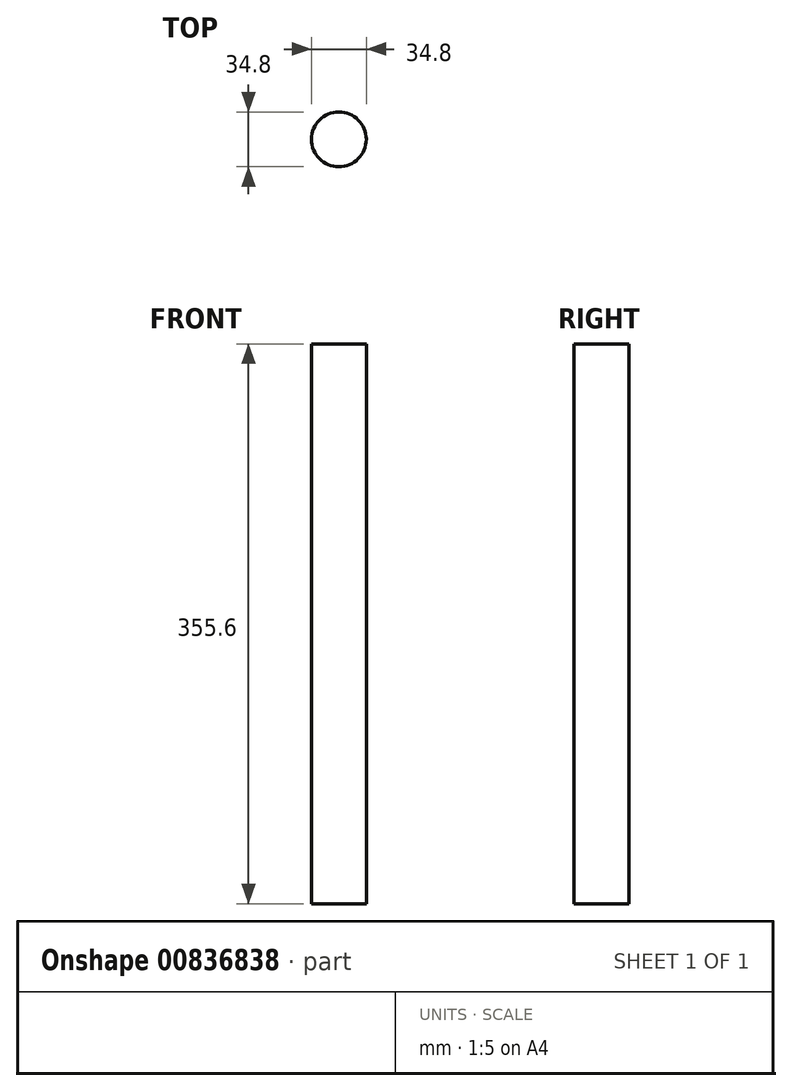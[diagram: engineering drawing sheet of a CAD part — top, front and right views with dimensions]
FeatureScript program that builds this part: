
annotation { "Feature Type Name" : "Feature", "Feature Type Description" : "" }
export const myFeature = defineFeature(function(context is Context, id is Id, definition is map)
    precondition{}
    {
        {
            var Q0;
            Q0=qCreatedBy(makeId("Top.planeOp"),FACE);
            var sketch = newSketch(context, id + "F0", { "sketchPlane" : qUnion([Q0])});
            skCircle(sketch, "E0", {"center": v(0, 0) * mm, "radius": 17.4 * mm});
            skSolve(sketch);
        }
        {
            var Q0;
            Q0=sQuery(id+"F0.wireOp",EDGE,"E0");
            extrude(context, id + "F1", {"bodyType" : ToolBodyType.SURFACE, "surfaceEntities" : qUnion([Q0]), "depth" : 355.6 * mm, "offsetDistance" : 25.4 * mm});
        }
    });
